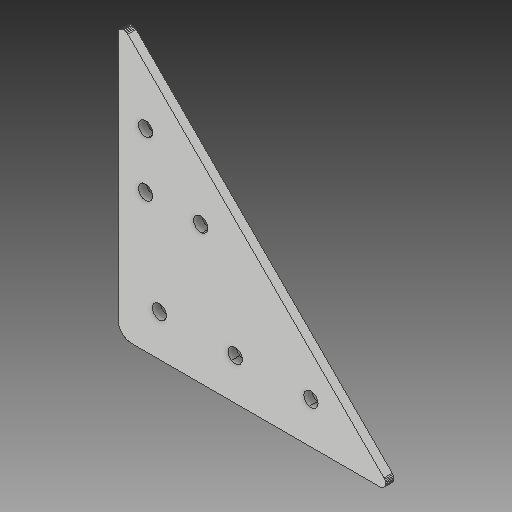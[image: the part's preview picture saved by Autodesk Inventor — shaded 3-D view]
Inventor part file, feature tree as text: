
AUTODESK INVENTOR PART (.ipt)
format: ipt  version: 2017 (Build 210142000, 142)  size: 230,912 bytes
history: native  units: mm
features: other x3, sketch x2, hole x1, projected_geometry x1
ambient origin geometry x8: Origin, YZ Plane, XZ Plane, XY Plane, X Axis, Y Axis, Z Axis, Center Point
bodies: Solid1 (feature_tree)
feature tree (7):
  other  "Side Brace.ipt"
  hole  "Hole1"  [1 undecoded]
  other  "Solid1::Side Brace.ipt"
  other  "TaggingFeature1"
  sketch  "Sketch1"  dims[d0=10.0mm]
  sketch  "Sketch2"  dims[d1=5.2mm d2=6.0mm d3=4.0mm d4=2.0mm d5=90.0deg d6=8.0mm d7=20.594885mm]
  projected_geometry  "Projected Loop1"
note: 1 required parameter value undecoded (feature->parameter linkage not recoverable at this tier; creation-order binding heuristic only, values carry confidence <= 0.55)
